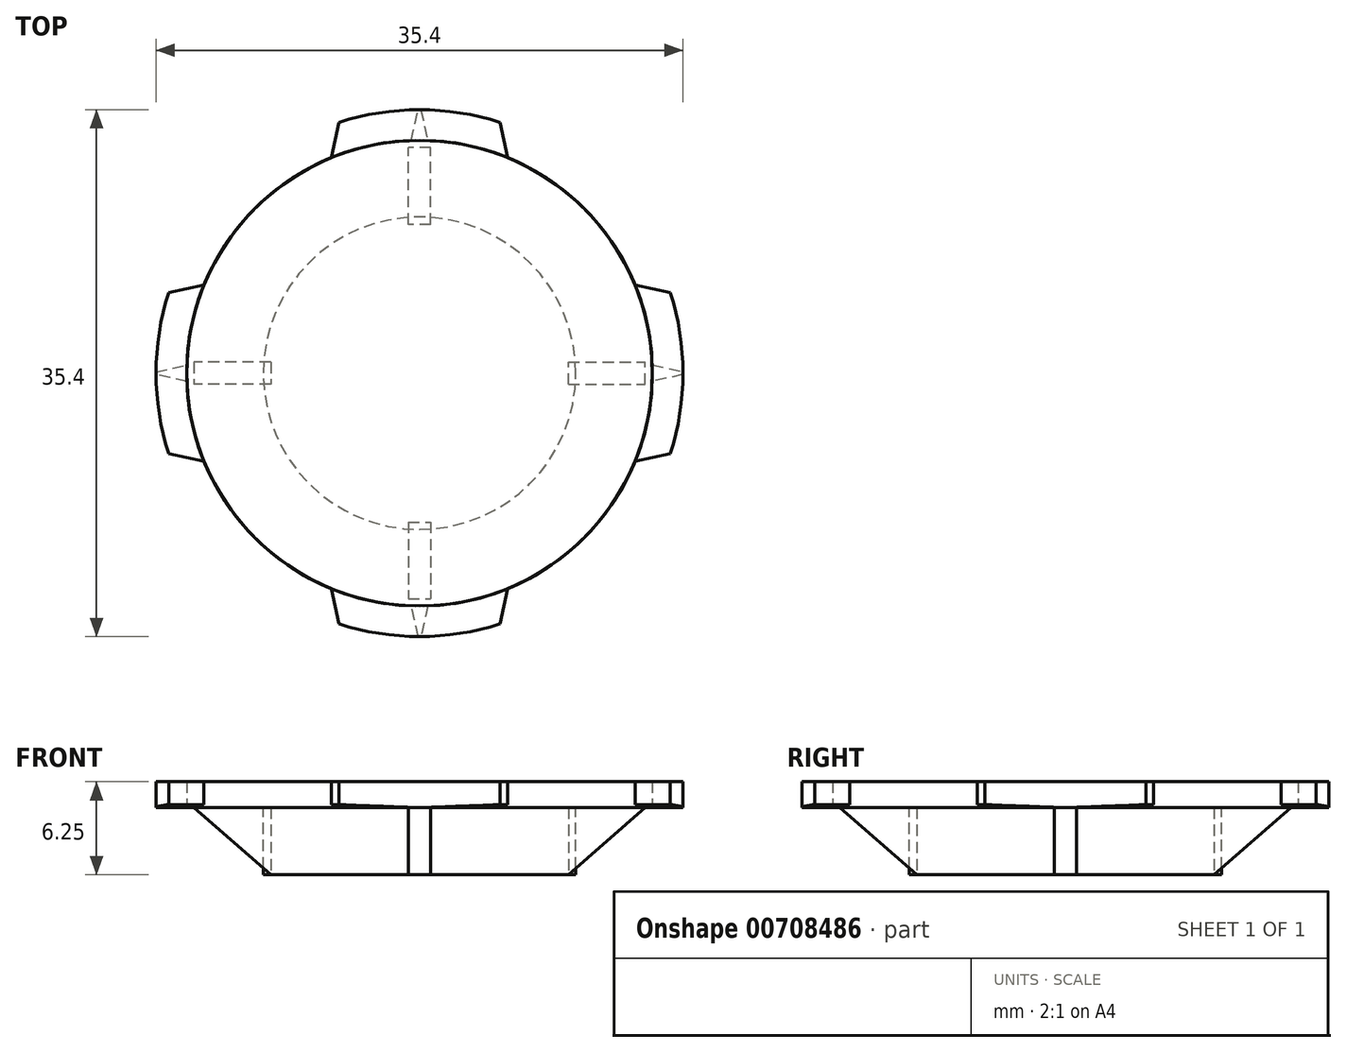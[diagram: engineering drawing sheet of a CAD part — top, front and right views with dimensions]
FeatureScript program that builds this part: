
annotation { "Feature Type Name" : "Feature", "Feature Type Description" : "" }
export const myFeature = defineFeature(function(context is Context, id is Id, definition is map)
    precondition{}
    {
        {
            var Q0;
            Q0=qCreatedBy(makeId("Top.planeOp"),FACE);
            var sketch = newSketch(context, id + "F0", { "sketchPlane" : qUnion([Q0])});
            skCircle(sketch, "E0", {"center": v(0, 0) * mm, "radius": 15.65 * mm});
            skArc(sketch, "E1", {"start": v(16.86, -5.4) * mm, "mid": v(17.7, 0) * mm, "end": v(16.86, 5.4) * mm});
            skLineSegment(sketch, "E2", {"start": v(0, 0) * mm, "end": v(17.7, 0) * mm, "construction": true});
            skLineSegment(sketch, "E3", {"start": v(16.86, -5.4) * mm, "end": v(14.48, -5.93) * mm});
            skLineSegment(sketch, "E4", {"start": v(16.86, 5.4) * mm, "end": v(14.48, 5.93) * mm});
            skSolve(sketch);
        }
        {
            var Q0;
            Q0 = qSketchRegion(id + "F0", true);
            extrude(context, id + "F1", {"entities" : qUnion([Q0]), "depth" : 1.75 * mm, "offsetDistance" : 25 * mm});
        }
        {
            var Q0;
            Q0=makeQuery(id+"F1.opExtrude","CAP_FACE",FACE,{"disambiguationData":[OSD([sQuery(id+"F0.wireOp",EDGE,"E0")])],"isStart":true});
            var sketch = newSketch(context, id + "F2", { "sketchPlane" : qUnion([Q0])});
            skCircle(sketch, "E5", {"center": v(0, 0) * mm, "radius": 10.5 * mm});
            skSolve(sketch);
        }
        {
            var Q0;
            Q0=makeQuery(id+"F2.imprint","IMPRINT",FACE,{"disambiguationData":[TD([[makeQuery(id+"F2.imprint","IMPRINT",EDGE,{"derivedFrom":sQuery(id+"F2.wireOp",EDGE,"E5")}),1.0]])]});
            var Q1;
            Q1=sQuery(id+"F2.wireOp",EDGE,"E5");
            extrude(context, id + "F3", {"entities" : qUnion([Q0]), "surfaceEntities" : qUnion([Q1]), "depth" : 4.5 * mm, "offsetDistance" : 25 * mm});
        }
        {
            var Q0;
            Q0=makeQuery(id+"F1.opExtrude","CAP_EDGE",EDGE,{"disambiguationData":[OSD([sQuery(id+"F0.wireOp",EDGE,"E4")])],"isStart":true});
            var Q1;
            Q1=makeQuery(id+"F1.opExtrude","CAP_EDGE",EDGE,{"disambiguationData":[OSD([sQuery(id+"F0.wireOp",EDGE,"E3")])],"isStart":true});
            chamfer(context, id + "F4", {"entities" : qUnion([Q0, Q1]), "chamferType" : ChamferType.TWO_OFFSETS, "width1" : .2 * mm, "oppositeDirection" : false, "width2" : 5 * mm, "tangentPropagation" : true});
        }
        {
            var Q0;
            Q0=qCreatedBy(makeId("Front.planeOp"),FACE);
            var sketch = newSketch(context, id + "F5", { "sketchPlane" : qUnion([Q0])});
            skLineSegment(sketch, "E6", {"start": v(10, 0) * mm, "end": v(15.15, 0) * mm});
            skLineSegment(sketch, "E7", {"start": v(10, 0) * mm, "end": v(10, -4.5) * mm});
            skLineSegment(sketch, "E8", {"start": v(10, -4.5) * mm, "end": v(15.15, 0) * mm});
            skLineSegment(sketch, "E9", {"start": v(10.5, -4.5) * mm, "end": v(10, -4.5) * mm, "construction": true});
            skLineSegment(sketch, "E10", {"start": v(15.15, 0) * mm, "end": v(15.65, 0) * mm, "construction": true});
            skLineSegment(sketch, "E11", {"start": v(0, -3.83) * mm, "end": v(0, -13.92) * mm, "construction": true});
            skLineSegment(sketch, "E12", {"start": v(0, -3.83) * mm, "end": v(0, 18.11) * mm, "construction": true});
            skSolve(sketch);
        }
        {
            var Q0;
            Q0=makeQuery(id+"F5.imprint","IMPRINT",FACE,{"disambiguationData":[TD([[makeQuery(id+"F5.imprint","IMPRINT",EDGE,{"derivedFrom":sQuery(id+"F5.wireOp",EDGE,"E6")}),-1.0]])]});
            extrude(context, id + "F6", {"entities" : qUnion([Q0]), "endBound" : BoundingType.SYMMETRIC, "depth" : 1.5 * mm, "offsetDistance" : 25 * mm});
        }
        {
            var Q0;
            Q0=makeQuery(id+"F6.opExtrude","SWEPT_BODY",BODY,{"disambiguationData":[OSD([sQuery(id+"F5.wireOp",EDGE,"E6"),sQuery(id+"F5.wireOp",EDGE,"E7"),sQuery(id+"F5.wireOp",EDGE,"E8")])]});
            var Q1;
            Q1=makeQuery(id+"F3.opExtrude","SWEPT_FACE",FACE,{"disambiguationData":[OSD([sQuery(id+"F2.wireOp",EDGE,"E5")])]});
            circularPattern(context, id + "F7", {"entities" : qUnion([Q0]), "axis" : qUnion([Q1]), "angle" : 360 * degree, "instanceCount" : 4, "equalSpace" : true});
        }
        {
            var Q0;
            Q0=makeQuery(id+"F1.opExtrude","SWEPT_BODY",BODY,{"disambiguationData":[OSD([sQuery(id+"F0.wireOp",EDGE,"E0"),sQuery(id+"F0.wireOp",EDGE,"E1"),sQuery(id+"F0.wireOp",EDGE,"E3"),sQuery(id+"F0.wireOp",EDGE,"E4"),sQuery(id+"F0.wireOp",EDGE,"49c069c4-aff0-4461-8faa-8bf6e7cc1451.1.0"),sQuery(id+"F0.wireOp",EDGE,"49c069c4-aff0-4461-8faa-8bf6e7cc1451.1.1"),sQuery(id+"F0.wireOp",EDGE,"49c069c4-aff0-4461-8faa-8bf6e7cc1451.1.2"),sQuery(id+"F0.wireOp",EDGE,"49c069c4-aff0-4461-8faa-8bf6e7cc1451.2.0"),sQuery(id+"F0.wireOp",EDGE,"49c069c4-aff0-4461-8faa-8bf6e7cc1451.2.1"),sQuery(id+"F0.wireOp",EDGE,"49c069c4-aff0-4461-8faa-8bf6e7cc1451.2.2"),sQuery(id+"F0.wireOp",EDGE,"49c069c4-aff0-4461-8faa-8bf6e7cc1451.3.0"),sQuery(id+"F0.wireOp",EDGE,"49c069c4-aff0-4461-8faa-8bf6e7cc1451.3.1"),sQuery(id+"F0.wireOp",EDGE,"49c069c4-aff0-4461-8faa-8bf6e7cc1451.3.2")])]});
            var Q1;
            Q1=makeQuery(id+"F3.opExtrude","SWEPT_FACE",FACE,{"disambiguationData":[OSD([sQuery(id+"F2.wireOp",EDGE,"E5")])]});
            circularPattern(context, id + "F8", {"entities" : qUnion([Q0]), "axis" : qUnion([Q1]), "angle" : 360 * degree, "instanceCount" : 4, "equalSpace" : true});
        }
    });
